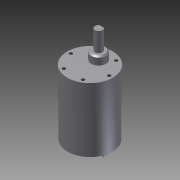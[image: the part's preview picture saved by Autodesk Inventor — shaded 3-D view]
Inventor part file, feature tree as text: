
AUTODESK INVENTOR PART (.ipt)
format: ipt  version: 2011 SP2 (Build 150309200, 309)  size: 164,352 bytes
history: native  units: mm
features: extrude x8, sketch x6, hole x1, pattern_circular x1, chamfer x1
ambient origin geometry x8: Origin, YZ Plane, XZ Plane, XY Plane, X Axis, Y Axis, Z Axis, Center Point
bodies: Solid1 (feature_tree)
feature tree (17):
  extrude  "Extrusion1"  Depth=22.0mm TaperAngle=0.0deg
  extrude  "Extrusion2"  Depth=30.0mm TaperAngle=0.0deg
  sketch  "Sketch3"  dims[d6=35.5mm d7=10.0mm]
  extrude  "Extrusion3"  Depth=10.0mm
  extrude  "Extrusion4"  Depth=4.0mm
  extrude  "Extrusion5"  Depth=1.0mm
  sketch  "Sketch4"  dims[d8=4.0mm d9=4.0mm]
  extrude  "Extrusion6"  Depth=2.0mm
  hole  "Hole1"  [1 undecoded]
  pattern_circular  "Circular Pattern1"  [2 undecoded]
  chamfer  "Chamfer1"  Distance=5.6mm
  extrude  "Extrusion7"  Depth=2.0mm TaperAngle=0.0deg
  extrude  "Extrusion8"  Depth=1.0mm TaperAngle=0.0deg
  sketch  "Sketch1"  dims[d0=36.8mm d1=22.0mm d2=0.0mm]
  sketch  "Sketch2"  dims[d3=36.0mm d4=30.0mm d5=0.0mm]
  sketch  "Sketch5"  dims[d10=1.0mm d11=1.0mm]
  sketch  "Sketch6"  dims[d12=2.0mm d13=2.0mm d14=12.0mm d15=12.0mm d16=5.6mm d17=0.0mm d18=2.0mm d19=0.0mm d20=1.0mm d21=0.0mm d22=7.0mm d23=12.0mm d24=6.5mm d25=0.0mm d28=15.5mm d29=2.621mm d30=7.0mm d31=4.0mm d32=2.0mm d33=90.0deg d34=8.0mm d35=20.594885mm d36=60.0mm d37=360.0deg d39=1.0mm d40=2.0mm d41=45.0deg d42=6.0mm d43=15.5mm d44=0.0mm d45=5.4mm d46=12.0mm d47=0.0mm]
note: 3 required parameter values undecoded (feature->parameter linkage not recoverable at this tier; creation-order binding heuristic only, values carry confidence <= 0.55)
